# Revit family: for update_36425USA_NEW
name_source: partatom
category: Plumbing Fixtures
revit_build: Autodesk Revit 2018 (Build: 20170223_1515(x64)
units: mm (PartAtom-declared; Revit-internal decimal feet)

## family parameters
Always vertical = No
Cut with Voids When Loaded = No
OmniClass Number = 23.31.11.00
OmniClass Title = Faucets
Part Type = Normal
Room Calculation Point = No
Round Connector Dimension = Use Diameter
Shared = No
Work Plane-Based = Yes

## types (2) — shared parameters
Always visible = Yes
BIMobject category = Taps & Mixers
Connector Description = Water Inlet 19.1mm
Default Elevation = 1219 mm
Description = AXOR Citterio E Bath spout
Design country = Germany
Diameter = 19 mm
EAN code = 4011097776965
Edition number = 1
IFC Classification = Valve
Manufacturer = AXOR
Manufacturer country = Germany
Manufacturer name = AXOR
Material main = Brass
Material secondary = Chrome
Model = 36425USA
OmniClass Code = 23-31 11 00
OmniClass Description = Faucets
Product Guid = b3935b4d-cf1f-4c1a-b575-63141be7eaec
Product SKU = 36425USA
Product data url = https://bimobject.com
Product family = AXOR Citterio E
Product group = Bath fillers
Product name = 36425USA AXOR Citterio E Bath spout
QR code = https://bimobject.com
URL = https://www.axor-design.com
Weight Net (Kg) = 0.9

## per-type parameters (varying)
| type | Material 1 |
| 001 Chrome | AXOR - Metal - 001 Chrome |
| 671 Matt Black | AXOR - Metal - 671 Matt Black |

## geometry (parser evidence)
native form markers: Sweep x1
no freeform markers — native parametric forms only
